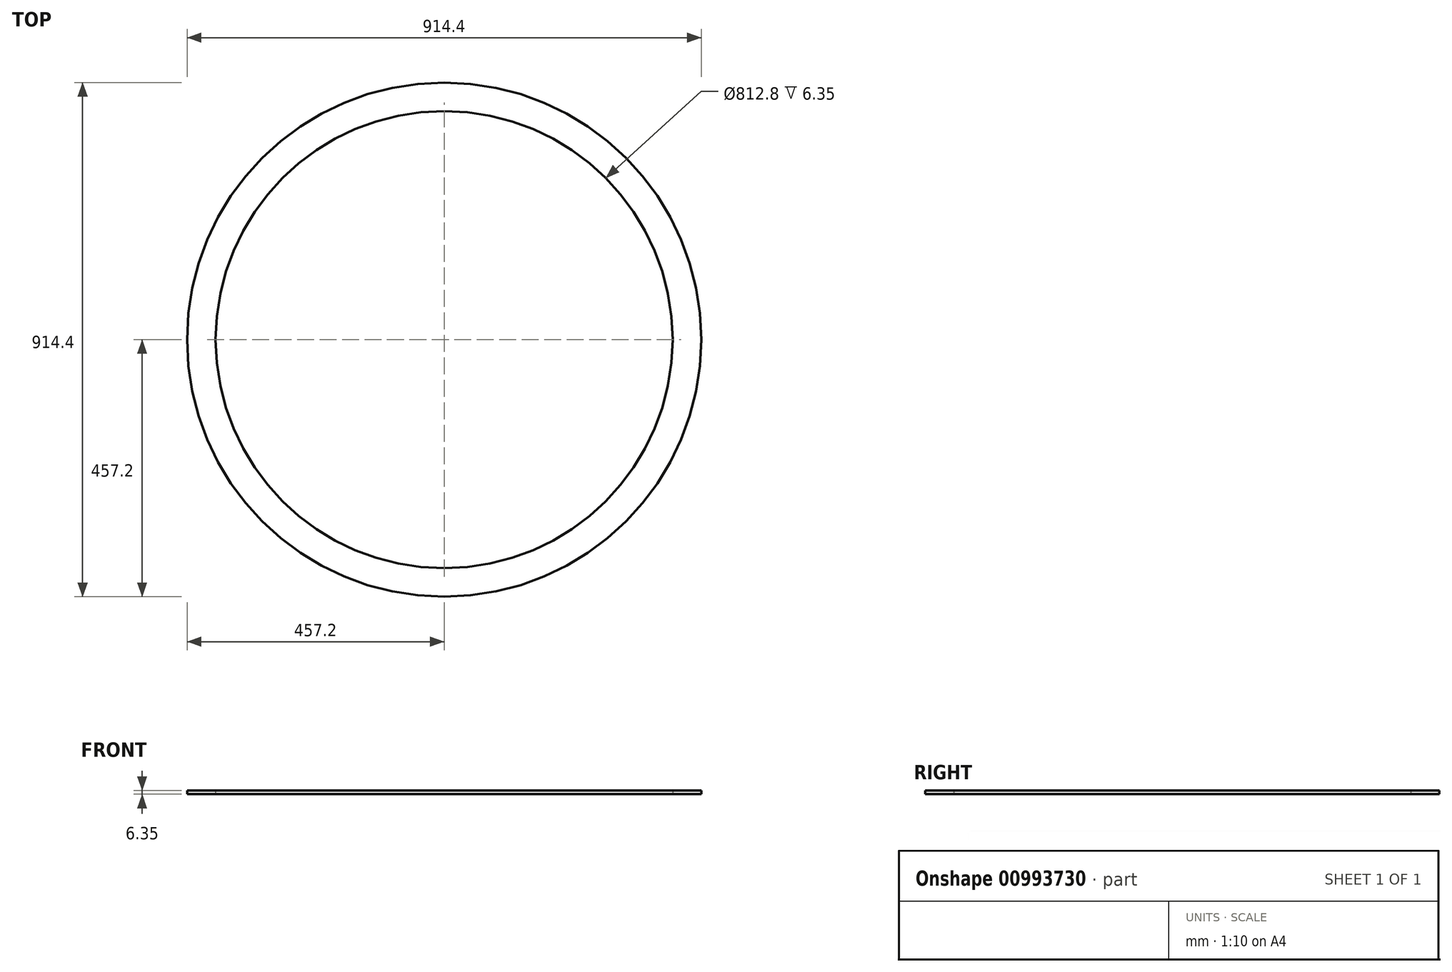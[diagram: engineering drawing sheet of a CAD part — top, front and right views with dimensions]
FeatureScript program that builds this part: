
annotation { "Feature Type Name" : "Feature", "Feature Type Description" : "" }
export const myFeature = defineFeature(function(context is Context, id is Id, definition is map)
    precondition{}
    {
        {
            var Q0;
            Q0=qCreatedBy(makeId("Top.planeOp"),FACE);
            var sketch = newSketch(context, id + "F0", { "sketchPlane" : qUnion([Q0])});
            skCircle(sketch, "E0", {"center": v(0, 0) * mm, "radius": 457.2 * mm});
            skCircle(sketch, "E1", {"center": v(0, 0) * mm, "radius": 406.4 * mm});
            skSolve(sketch);
        }
        {
            var Q0;
            Q0=makeQuery(id+"F0.imprint","IMPRINT",FACE,{"disambiguationData":[TD([[makeQuery(id+"F0.imprint","IMPRINT",EDGE,{"derivedFrom":sQuery(id+"F0.wireOp",EDGE,"E0")}),1.0]])]});
            extrude(context, id + "F1", {"entities" : qUnion([Q0]), "depth" : 6.35 * mm, "offsetDistance" : 25.4 * mm});
        }
    });
